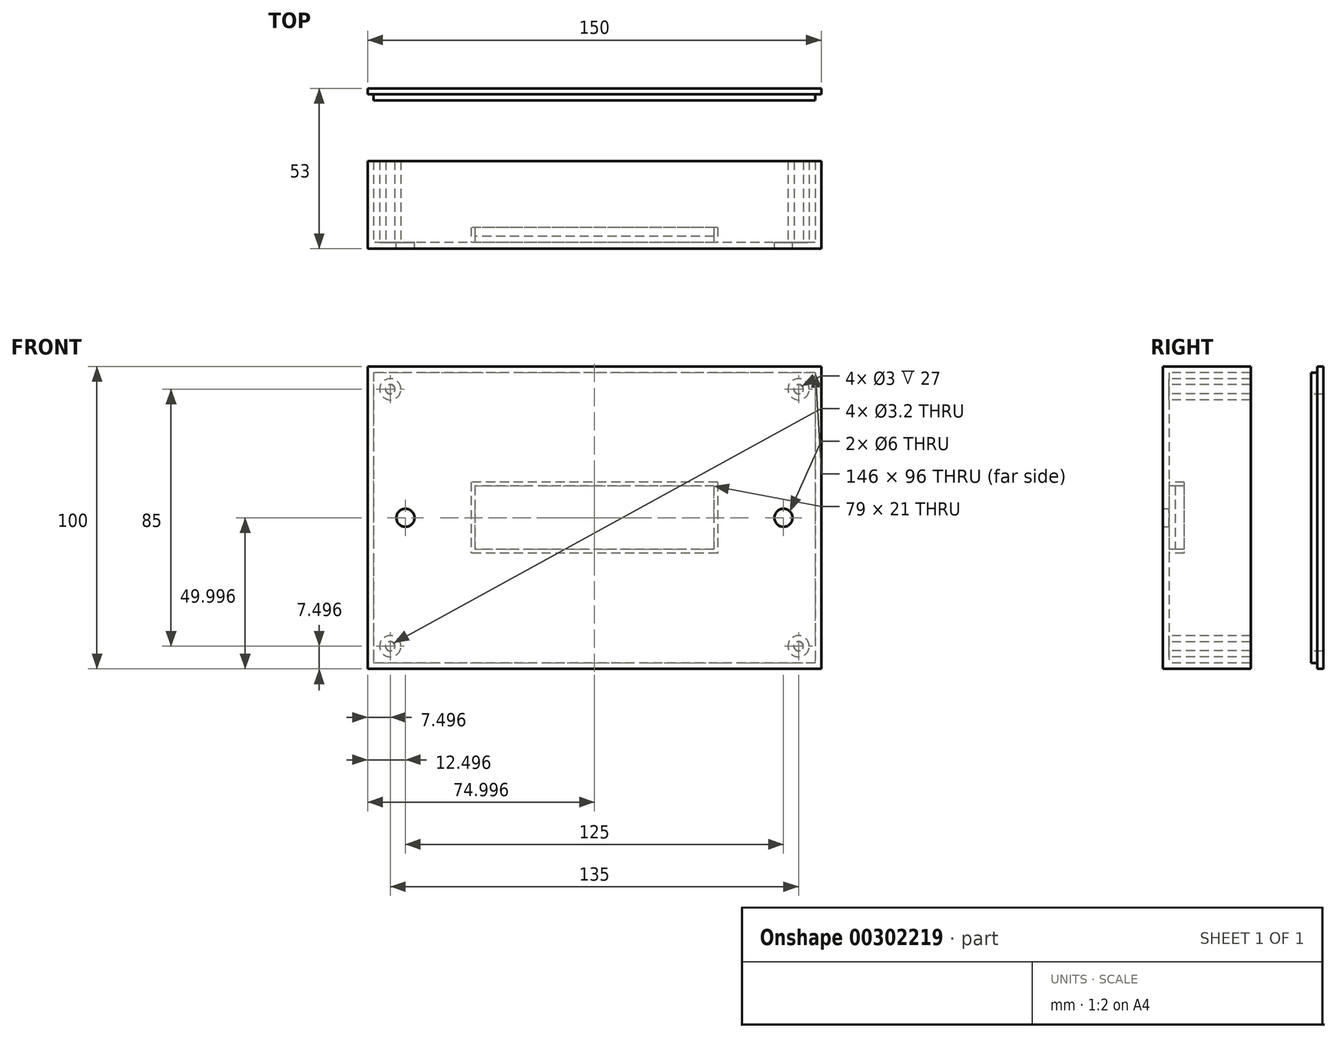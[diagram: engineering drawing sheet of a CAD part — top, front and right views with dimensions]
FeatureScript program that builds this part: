
annotation { "Feature Type Name" : "Feature", "Feature Type Description" : "" }
export const myFeature = defineFeature(function(context is Context, id is Id, definition is map)
    precondition{}
    {
        {
            var Q0;
            Q0=qCreatedBy(makeId("Front.planeOp"),FACE);
            var sketch = newSketch(context, id + "F0", { "sketchPlane" : qUnion([Q0])});
            skLineSegment(sketch, "E0.bottom", {"start": v(-13.24, 172.25) * mm, "end": v(136.76, 172.25) * mm});
            skLineSegment(sketch, "E0.top", {"start": v(-13.24, 72.25) * mm, "end": v(136.76, 72.25) * mm});
            skLineSegment(sketch, "E0.left", {"start": v(-13.24, 172.25) * mm, "end": v(-13.24, 72.25) * mm});
            skLineSegment(sketch, "E0.right", {"start": v(136.76, 172.25) * mm, "end": v(136.76, 72.25) * mm});
            skPoint(sketch, "E1", {"position": v(-13.24, 122.25) * mm});
            skPoint(sketch, "E2", {"position": v(136.76, 122.25) * mm});
            skCircle(sketch, "E3", {"center": v(-0.74, 122.25) * mm, "radius": 3 * mm});
            skCircle(sketch, "E4", {"center": v(124.26, 122.25) * mm, "radius": 3 * mm});
            skLineSegment(sketch, "E5.bottom", {"start": v(101.26, 132.75) * mm, "end": v(22.26, 132.75) * mm});
            skLineSegment(sketch, "E5.top", {"start": v(101.26, 111.75) * mm, "end": v(22.26, 111.75) * mm});
            skLineSegment(sketch, "E5.left", {"start": v(101.26, 132.75) * mm, "end": v(101.26, 111.75) * mm});
            skLineSegment(sketch, "E5.right", {"start": v(22.26, 132.75) * mm, "end": v(22.26, 111.75) * mm});
            skPoint(sketch, "E5.middle", {"position": v(61.76, 122.25) * mm});
            skPoint(sketch, "E6", {"position": v(61.76, 172.25) * mm});
            skLineSegment(sketch, "E7.bottom", {"start": v(102.5, 134) * mm, "end": v(21, 134) * mm});
            skLineSegment(sketch, "E7.top", {"start": v(102.5, 110.5) * mm, "end": v(21, 110.5) * mm});
            skLineSegment(sketch, "E7.left", {"start": v(102.5, 134) * mm, "end": v(102.5, 110.5) * mm});
            skLineSegment(sketch, "E7.right", {"start": v(21, 134) * mm, "end": v(21, 110.5) * mm});
            skLineSegment(sketch, "E8.bottom", {"start": v(134.76, 170.25) * mm, "end": v(-11.24, 170.25) * mm});
            skLineSegment(sketch, "E8.top", {"start": v(134.76, 74.25) * mm, "end": v(-11.24, 74.25) * mm});
            skLineSegment(sketch, "E8.left", {"start": v(134.76, 170.25) * mm, "end": v(134.76, 74.25) * mm});
            skLineSegment(sketch, "E8.right", {"start": v(-11.24, 170.25) * mm, "end": v(-11.24, 74.25) * mm});
            skCircle(sketch, "E9", {"center": v(129.26, 164.75) * mm, "radius": 3.5 * mm});
            skCircle(sketch, "E10", {"center": v(129.26, 164.75) * mm, "radius": 1.5 * mm});
            skCircle(sketch, "E11", {"center": v(129.26, 79.75) * mm, "radius": 3.5 * mm});
            skCircle(sketch, "E12", {"center": v(129.26, 79.75) * mm, "radius": 1.5 * mm});
            skCircle(sketch, "E13", {"center": v(-5.74, 79.75) * mm, "radius": 3.5 * mm});
            skCircle(sketch, "E14", {"center": v(-5.74, 79.75) * mm, "radius": 1.5 * mm});
            skCircle(sketch, "E15", {"center": v(-5.74, 164.75) * mm, "radius": 3.5 * mm});
            skCircle(sketch, "E16", {"center": v(-5.74, 164.75) * mm, "radius": 1.5 * mm});
            skSolve(sketch);
        }
        {
            var Q0;
            Q0=makeQuery(id+"F0.imprint","IMPRINT",FACE,{"disambiguationData":[TD([[makeQuery(id+"F0.imprint","IMPRINT",EDGE,{"derivedFrom":sQuery(id+"F0.wireOp",EDGE,"E5.bottom")}),-1.0]])]});
            extrude(context, id + "F1", {"entities" : qUnion([Q0]), "oppositeDirection" : true, "depth" : 5 * mm, "offsetDistance" : 25 * mm});
        }
        {
            var Q0;
            Q0=makeQuery(id+"F0.imprint","IMPRINT",FACE,{"disambiguationData":[TD([[makeQuery(id+"F0.imprint","IMPRINT",EDGE,{"derivedFrom":sQuery(id+"F0.wireOp",EDGE,"E0.bottom")}),-1.0]])]});
            var Q1;
            Q1=makeQuery(id+"F0.imprint","IMPRINT",FACE,{"disambiguationData":[TD([[makeQuery(id+"F0.imprint","IMPRINT",EDGE,{"derivedFrom":sQuery(id+"F0.wireOp",EDGE,"E5.bottom")}),1.0]])]});
            var Q2;
            Q2=makeQuery(id+"F0.imprint","IMPRINT",FACE,{"disambiguationData":[TD([[makeQuery(id+"F0.imprint","IMPRINT",EDGE,{"derivedFrom":sQuery(id+"F0.wireOp",EDGE,"E5.bottom")}),-1.0]])]});
            var Q3;
            Q3=makeQuery(id+"F0.imprint","IMPRINT",FACE,{"disambiguationData":[TD([[makeQuery(id+"F0.imprint","IMPRINT",EDGE,{"derivedFrom":sQuery(id+"F0.wireOp",EDGE,"E14")}),1.0]])]});
            var Q4;
            Q4=makeQuery(id+"F0.imprint","IMPRINT",FACE,{"disambiguationData":[TD([[makeQuery(id+"F0.imprint","IMPRINT",EDGE,{"derivedFrom":sQuery(id+"F0.wireOp",EDGE,"E13")}),1.0]])]});
            var Q5;
            Q5=makeQuery(id+"F0.imprint","IMPRINT",FACE,{"disambiguationData":[TD([[makeQuery(id+"F0.imprint","IMPRINT",EDGE,{"derivedFrom":sQuery(id+"F0.wireOp",EDGE,"E3")}),-1.0]])]});
            var Q6;
            Q6=makeQuery(id+"F0.imprint","IMPRINT",FACE,{"disambiguationData":[TD([[makeQuery(id+"F0.imprint","IMPRINT",EDGE,{"derivedFrom":sQuery(id+"F0.wireOp",EDGE,"E10")}),1.0]])]});
            var Q7;
            Q7=makeQuery(id+"F0.imprint","IMPRINT",FACE,{"disambiguationData":[TD([[makeQuery(id+"F0.imprint","IMPRINT",EDGE,{"derivedFrom":sQuery(id+"F0.wireOp",EDGE,"E9")}),1.0]])]});
            var Q8;
            Q8=makeQuery(id+"F0.imprint","IMPRINT",FACE,{"disambiguationData":[TD([[makeQuery(id+"F0.imprint","IMPRINT",EDGE,{"derivedFrom":sQuery(id+"F0.wireOp",EDGE,"E11")}),1.0]])]});
            var Q9;
            Q9=makeQuery(id+"F0.imprint","IMPRINT",FACE,{"disambiguationData":[TD([[makeQuery(id+"F0.imprint","IMPRINT",EDGE,{"derivedFrom":sQuery(id+"F0.wireOp",EDGE,"E12")}),1.0]])]});
            var Q10;
            Q10=makeQuery(id+"F0.imprint","IMPRINT",FACE,{"disambiguationData":[TD([[makeQuery(id+"F0.imprint","IMPRINT",EDGE,{"derivedFrom":sQuery(id+"F0.wireOp",EDGE,"E15")}),1.0]])]});
            var Q11;
            Q11=makeQuery(id+"F0.imprint","IMPRINT",FACE,{"disambiguationData":[TD([[makeQuery(id+"F0.imprint","IMPRINT",EDGE,{"derivedFrom":sQuery(id+"F0.wireOp",EDGE,"E16")}),1.0]])]});
            extrude(context, id + "F2", {"entities" : qUnion([Q0, Q1, Q2, Q3, Q4, Q5, Q6, Q7, Q8, Q9, Q10, Q11]), "depth" : 2 * mm, "offsetDistance" : 25 * mm});
        }
        {
            var Q0;
            Q0 = qSketchRegion(id + "F0", true);
            var Q1;
            Q1=makeQuery(id+"F0.imprint","IMPRINT",FACE,{"disambiguationData":[TD([[makeQuery(id+"F0.imprint","IMPRINT",EDGE,{"derivedFrom":sQuery(id+"F0.wireOp",EDGE,"E9")}),1.0]])]});
            var Q2;
            Q2=makeQuery(id+"F0.imprint","IMPRINT",FACE,{"disambiguationData":[TD([[makeQuery(id+"F0.imprint","IMPRINT",EDGE,{"derivedFrom":sQuery(id+"F0.wireOp",EDGE,"E15")}),1.0]])]});
            var Q3;
            Q3=makeQuery(id+"F0.imprint","IMPRINT",FACE,{"disambiguationData":[TD([[makeQuery(id+"F0.imprint","IMPRINT",EDGE,{"derivedFrom":sQuery(id+"F0.wireOp",EDGE,"E13")}),1.0]])]});
            var Q4;
            Q4=makeQuery(id+"F0.imprint","IMPRINT",FACE,{"disambiguationData":[TD([[makeQuery(id+"F0.imprint","IMPRINT",EDGE,{"derivedFrom":sQuery(id+"F0.wireOp",EDGE,"E11")}),1.0]])]});
            extrude(context, id + "F3", {"entities" : qUnion([Q0, Q1, Q2, Q3, Q4]), "operationType" : NewBodyOperationType.ADD, "oppositeDirection" : true, "depth" : 27 * mm, "offsetDistance" : 25 * mm});
        }
        {
            var Q0;
            Q0=qCreatedBy(makeId("Front.planeOp"),FACE);
            cPlane(context, id + "F4", {"entities" : qUnion([Q0]), "cplaneType" : CPlaneType.OFFSET, "offset" : 49 * mm, "oppositeDirection" : true, "width" : 150 * mm, "height" : 150 * mm});
        }
        {
            var Q0;
            Q0=qCreatedBy(id+"F4.planeOp",FACE);
            var sketch = newSketch(context, id + "F5", { "sketchPlane" : qUnion([Q0])});
            skLineSegment(sketch, "E17.bottom", {"start": v(134.76, 170.25) * mm, "end": v(-11.24, 170.25) * mm});
            skLineSegment(sketch, "E17.top", {"start": v(134.76, 74.25) * mm, "end": v(-11.24, 74.25) * mm});
            skLineSegment(sketch, "E17.left", {"start": v(134.76, 170.25) * mm, "end": v(134.76, 74.25) * mm});
            skLineSegment(sketch, "E17.right", {"start": v(-11.24, 170.25) * mm, "end": v(-11.24, 74.25) * mm});
            skPoint(sketch, "E17.middle", {"position": v(61.76, 122.25) * mm});
            skCircle(sketch, "E18", {"center": v(129.26, 164.75) * mm, "radius": 1.6 * mm});
            skCircle(sketch, "E19", {"center": v(-5.74, 164.75) * mm, "radius": 1.6 * mm});
            skCircle(sketch, "E20", {"center": v(-5.74, 79.75) * mm, "radius": 1.6 * mm});
            skCircle(sketch, "E21", {"center": v(129.26, 79.75) * mm, "radius": 1.6 * mm});
            skLineSegment(sketch, "E22.bottom", {"start": v(-13.24, 172.25) * mm, "end": v(136.76, 172.25) * mm});
            skLineSegment(sketch, "E22.top", {"start": v(-13.24, 72.25) * mm, "end": v(136.76, 72.25) * mm});
            skLineSegment(sketch, "E22.left", {"start": v(-13.24, 172.25) * mm, "end": v(-13.24, 72.25) * mm});
            skLineSegment(sketch, "E22.right", {"start": v(136.76, 172.25) * mm, "end": v(136.76, 72.25) * mm});
            skSolve(sketch);
        }
        {
            var Q0;
            Q0=makeQuery(id+"F5.imprint","IMPRINT",FACE,{"disambiguationData":[TD([[makeQuery(id+"F5.imprint","IMPRINT",EDGE,{"derivedFrom":sQuery(id+"F5.wireOp",EDGE,"E17.bottom")}),1.0]])]});
            var Q1;
            Q1=makeQuery(id+"F5.imprint","IMPRINT",FACE,{"disambiguationData":[TD([[makeQuery(id+"F5.imprint","IMPRINT",EDGE,{"derivedFrom":sQuery(id+"F5.wireOp",EDGE,"E17.bottom")}),-1.0]])]});
            extrude(context, id + "F6", {"entities" : qUnion([Q0, Q1]), "oppositeDirection" : true, "depth" : 2 * mm, "offsetDistance" : 25 * mm});
        }
        {
            var Q0;
            Q0=makeQuery(id+"F5.imprint","IMPRINT",FACE,{"disambiguationData":[TD([[makeQuery(id+"F5.imprint","IMPRINT",EDGE,{"derivedFrom":sQuery(id+"F5.wireOp",EDGE,"E17.bottom")}),1.0]])]});
            extrude(context, id + "F7", {"entities" : qUnion([Q0]), "operationType" : NewBodyOperationType.ADD, "depth" : 2 * mm, "offsetDistance" : 25 * mm});
        }
        {
            var Q0;
            Q0=makeQuery(id+"F0.imprint","IMPRINT",FACE,{"disambiguationData":[TD([[makeQuery(id+"F0.imprint","IMPRINT",EDGE,{"derivedFrom":sQuery(id+"F0.wireOp",EDGE,"E5.bottom")}),1.0]])]});
            extrude(context, id + "F8", {"entities" : qUnion([Q0]), "oppositeDirection" : true, "depth" : 2 * mm, "offsetDistance" : 25 * mm});
        }
    });
